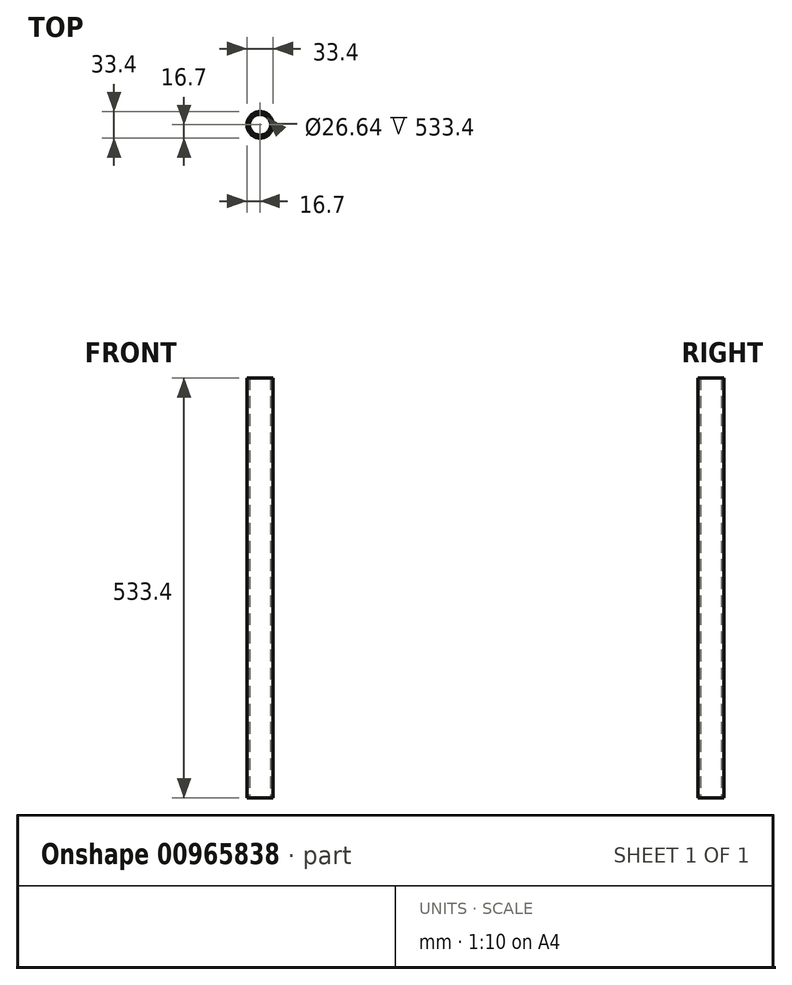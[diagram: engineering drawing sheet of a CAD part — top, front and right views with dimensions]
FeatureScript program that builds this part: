
annotation { "Feature Type Name" : "Feature", "Feature Type Description" : "" }
export const myFeature = defineFeature(function(context is Context, id is Id, definition is map)
    precondition{}
    {
        {
            var Q0;
            Q0=qCreatedBy(makeId("Top.planeOp"),FACE);
            var sketch = newSketch(context, id + "F0", { "sketchPlane" : qUnion([Q0])});
            skCircle(sketch, "E0", {"center": v(0, 0) * mm, "radius": 16.7 * mm});
            skCircle(sketch, "E1", {"center": v(0, 0) * mm, "radius": 13.32 * mm});
            skSolve(sketch);
        }
        {
            var Q0;
            Q0=makeQuery(id+"F0.imprint","IMPRINT",FACE,{"disambiguationData":[TD([[makeQuery(id+"F0.imprint","IMPRINT",EDGE,{"derivedFrom":sQuery(id+"F0.wireOp",EDGE,"E0")}),1.0]])]});
            extrude(context, id + "F1", {"entities" : qUnion([Q0]), "depth" : 533.4 * mm, "offsetDistance" : 25.4 * mm});
        }
    });
